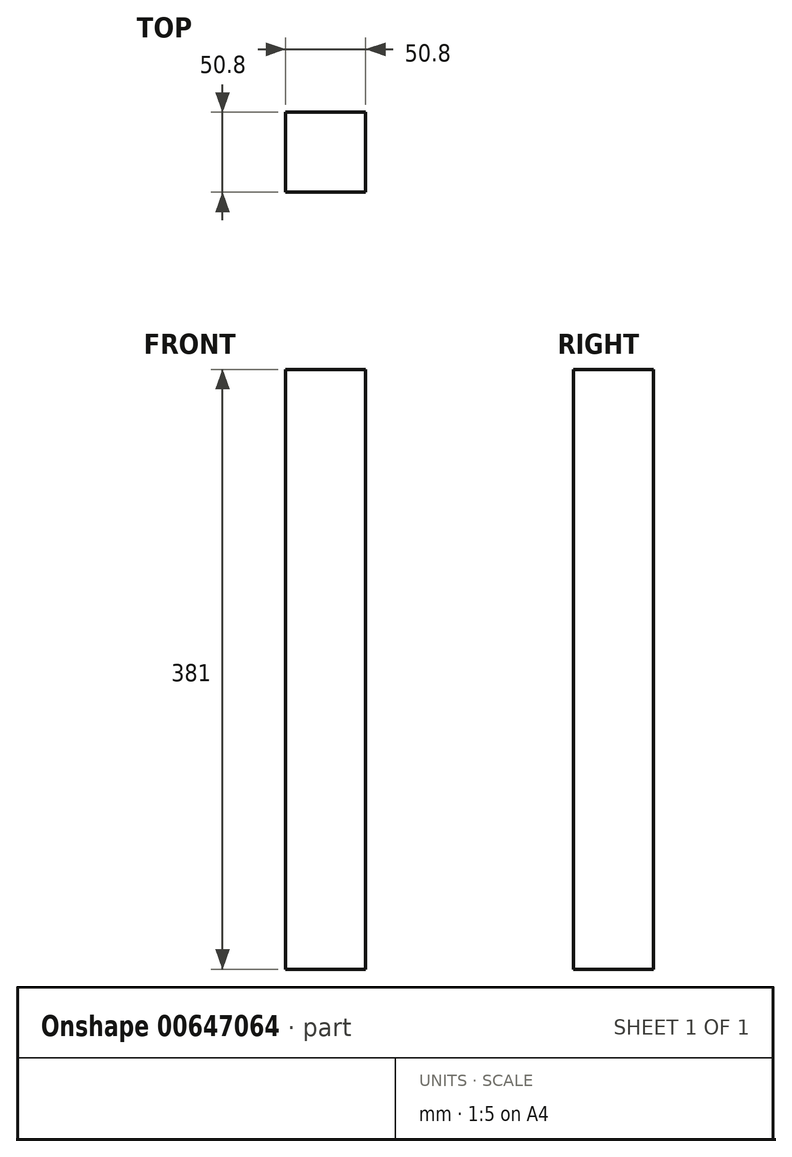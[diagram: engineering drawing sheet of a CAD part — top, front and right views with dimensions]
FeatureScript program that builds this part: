
annotation { "Feature Type Name" : "Feature", "Feature Type Description" : "" }
export const myFeature = defineFeature(function(context is Context, id is Id, definition is map)
    precondition{}
    {
        {
            var Q0;
            Q0=qCreatedBy(makeId("Top.planeOp"),FACE);
            var sketch = newSketch(context, id + "F0", { "sketchPlane" : qUnion([Q0])});
            skLineSegment(sketch, "E0.bottom", {"start": v(25.4, 25.4) * mm, "end": v(-25.4, 25.4) * mm});
            skLineSegment(sketch, "E0.top", {"start": v(25.4, -25.4) * mm, "end": v(-25.4, -25.4) * mm});
            skLineSegment(sketch, "E0.left", {"start": v(25.4, 25.4) * mm, "end": v(25.4, -25.4) * mm});
            skLineSegment(sketch, "E0.right", {"start": v(-25.4, 25.4) * mm, "end": v(-25.4, -25.4) * mm});
            skPoint(sketch, "E0.middle", {"position": v(0, 0) * mm});
            skSolve(sketch);
        }
        {
            var Q0;
            Q0=makeQuery(id+"F0.imprint","IMPRINT",FACE,{"disambiguationData":[TD([[makeQuery(id+"F0.imprint","IMPRINT",EDGE,{"derivedFrom":sQuery(id+"F0.wireOp",EDGE,"E0.bottom")}),1.0]])]});
            extrude(context, id + "F1", {"entities" : qUnion([Q0]), "oppositeDirection" : true, "depth" : 381 * mm, "offsetDistance" : 25.4 * mm});
        }
    });
